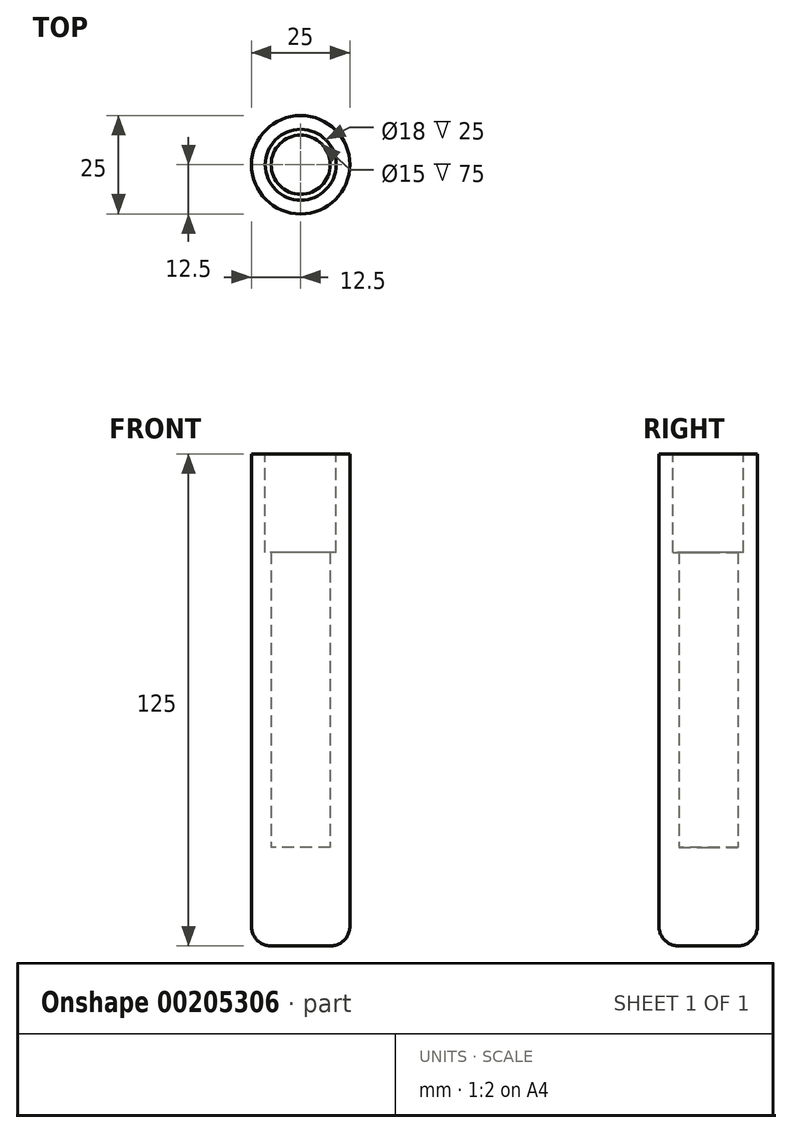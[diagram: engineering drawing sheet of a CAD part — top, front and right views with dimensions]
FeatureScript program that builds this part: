
annotation { "Feature Type Name" : "Feature", "Feature Type Description" : "" }
export const myFeature = defineFeature(function(context is Context, id is Id, definition is map)
    precondition{}
    {
        {
            var Q0;
            Q0=qCreatedBy(makeId("Top.planeOp"),FACE);
            var sketch = newSketch(context, id + "F0", { "sketchPlane" : qUnion([Q0])});
            skCircle(sketch, "E0", {"center": v(0, 0) * mm, "radius": 7.5 * mm});
            skCircle(sketch, "E1", {"center": v(0, 0) * mm, "radius": 12.5 * mm});
            skSolve(sketch);
        }
        {
            var Q0;
            Q0=makeQuery(id+"F0.imprint","IMPRINT",FACE,{"disambiguationData":[TD([[makeQuery(id+"F0.imprint","IMPRINT",EDGE,{"derivedFrom":sQuery(id+"F0.wireOp",EDGE,"E0")}),-1.0]])]});
            extrude(context, id + "F1", {"entities" : qUnion([Q0]), "depth" : 100 * mm});
        }
        {
            var Q0;
            Q0=makeQuery(id+"F1.opExtrude","CAP_FACE",FACE,{"disambiguationData":[OSD([sQuery(id+"F0.wireOp",EDGE,"E0"),sQuery(id+"F0.wireOp",EDGE,"E1")])],"isStart":true});
            var sketch = newSketch(context, id + "F2", { "sketchPlane" : qUnion([Q0])});
            skCircle(sketch, "E2.0", {"center": v(0, 0) * mm, "radius": 12.5 * mm});
            skSolve(sketch);
        }
        {
            var Q0;
            Q0 = qSketchRegion(id + "F2", true);
            extrude(context, id + "F3", {"entities" : qUnion([Q0]), "operationType" : NewBodyOperationType.ADD, "depth" : 25 * mm});
        }
        {
            var Q0;
            Q0=makeQuery(id+"F3.opExtrude","CAP_EDGE",EDGE,{"disambiguationData":[OSD([sQuery(id+"F2.wireOp",EDGE,"E2.0")])],"isStart":false});
            var Q1;
            Q1=makeQuery(id+"F1.opExtrude","CAP_EDGE",EDGE,{"disambiguationData":[OSD([sQuery(id+"F0.wireOp",EDGE,"E0")])],"isStart":true});
            fillet(context, id + "F4", {"entities" : qUnion([Q0, Q1]), "radius" : 5 * mm, "tangentPropagation" : true, "allowEdgeOverflow" : false});
        }
        {
            var Q0;
            Q0=makeQuery(id+"F1.opExtrude","CAP_FACE",FACE,{"disambiguationData":[OSD([sQuery(id+"F0.wireOp",EDGE,"E0"),sQuery(id+"F0.wireOp",EDGE,"E1")])],"isStart":false});
            var sketch = newSketch(context, id + "F5", { "sketchPlane" : qUnion([Q0])});
            skCircle(sketch, "E3", {"center": v(0, 0) * mm, "radius": 9 * mm});
            skSolve(sketch);
        }
        {
            var Q0;
            Q0=makeQuery(id+"F5.imprint","IMPRINT",FACE,{"disambiguationData":[TD([[makeQuery(id+"F5.imprint","IMPRINT",EDGE,{"derivedFrom":sQuery(id+"F5.wireOp",EDGE,"E3")}),1.0]])]});
            extrude(context, id + "F6", {"entities" : qUnion([Q0]), "operationType" : NewBodyOperationType.REMOVE, "oppositeDirection" : true, "depth" : 25 * mm});
        }
    });
